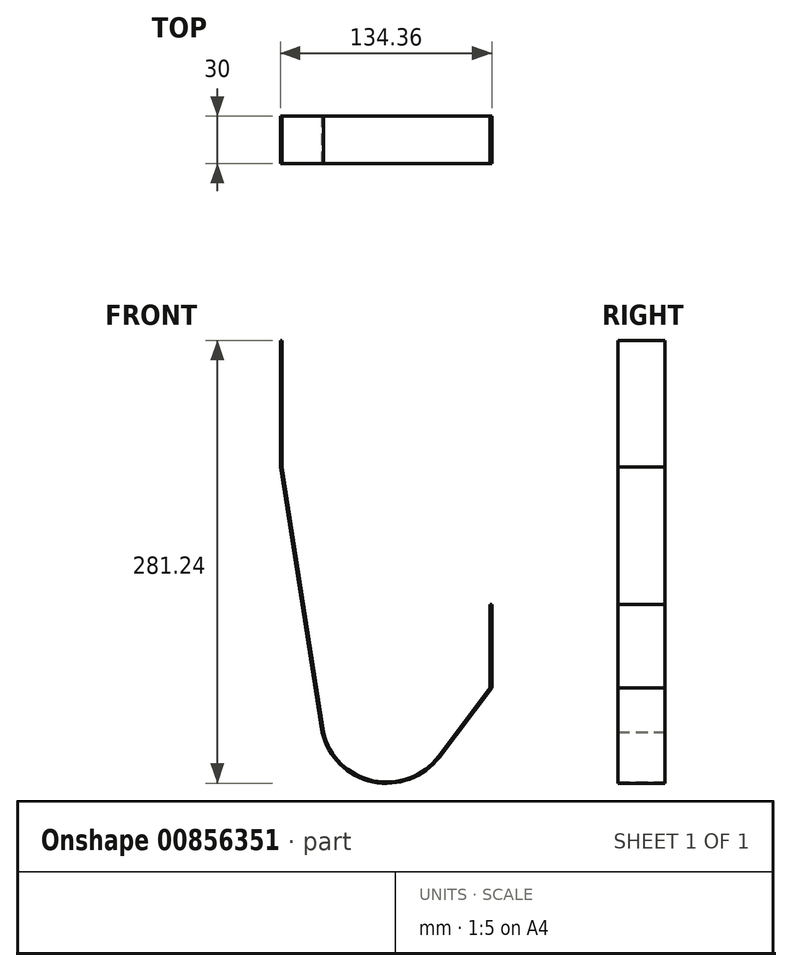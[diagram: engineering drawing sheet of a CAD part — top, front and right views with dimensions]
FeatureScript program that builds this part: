
annotation { "Feature Type Name" : "Feature", "Feature Type Description" : "" }
export const myFeature = defineFeature(function(context is Context, id is Id, definition is map)
    precondition{}
    {
        {
            var Q0;
            Q0=qCreatedBy(makeId("Front.planeOp"),FACE);
            var sketch = newSketch(context, id + "F0", { "sketchPlane" : qUnion([Q0])});
            skLineSegment(sketch, "E0", {"start": v(67.68, -1.52) * mm, "end": v(67.68, -54.57) * mm});
            skLineSegment(sketch, "E1", {"start": v(67.68, -54.57) * mm, "end": v(34.9, -97.88) * mm});
            skLineSegment(sketch, "E2", {"start": v(68.88, -1.52) * mm, "end": v(68.88, -54.57) * mm});
            skLineSegment(sketch, "E3", {"start": v(68.88, -54.57) * mm, "end": v(35.45, -98.45) * mm});
            skLineSegment(sketch, "E4", {"start": v(-64.42, 166.2) * mm, "end": v(-64.42, 85.79) * mm});
            skLineSegment(sketch, "E5", {"start": v(-64.42, 85.79) * mm, "end": v(-38.21, -82.52) * mm});
            skLineSegment(sketch, "E6", {"start": v(-64.42, 166.2) * mm, "end": v(-65.48, 166.2) * mm});
            skLineSegment(sketch, "E7", {"start": v(-65.48, 166.2) * mm, "end": v(-65.48, 85.86) * mm});
            skLineSegment(sketch, "E8", {"start": v(-65.48, 85.86) * mm, "end": v(-38.98, -82.54) * mm});
            skArc(sketch, "E9", {"start": v(-38.21, -82.52) * mm, "mid": v(-6.53, -113.38) * mm, "end": v(34.9, -97.88) * mm});
            skArc(sketch, "E10", {"start": v(-38.98, -82.54) * mm, "mid": v(-6.81, -114.1) * mm, "end": v(35.45, -98.45) * mm});
            skLineSegment(sketch, "E11", {"start": v(67.68, -1.52) * mm, "end": v(68.88, -1.52) * mm});
            skSolve(sketch);
        }
        {
            var Q0;
            Q0=makeQuery(id+"F0.imprint","IMPRINT",FACE,{"disambiguationData":[TD([[makeQuery(id+"F0.imprint","IMPRINT",EDGE,{"derivedFrom":sQuery(id+"F0.wireOp",EDGE,"E0")}),1.0]])]});
            extrude(context, id + "F1", {"entities" : qUnion([Q0]), "depth" : 30 * mm, "offsetDistance" : 25 * mm});
        }
    });
